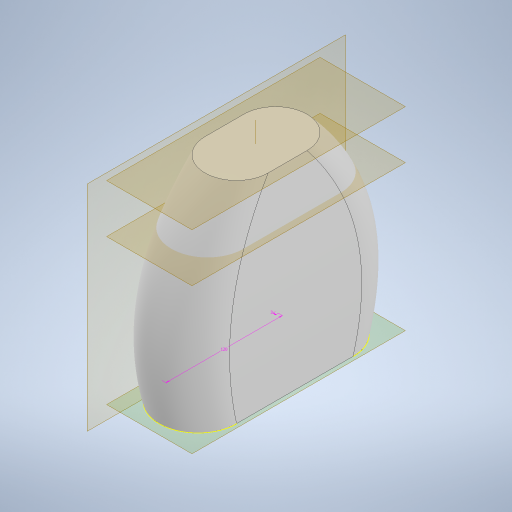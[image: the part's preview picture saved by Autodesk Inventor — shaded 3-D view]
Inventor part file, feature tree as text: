
AUTODESK INVENTOR PART (.ipt)
format: ipt  version: 2023 (Build 270158000, 158)  size: 420,864 bytes
history: native  units: mm
features: sketch x4, plane x4, loft x1, shell x1, extrude x1, projected_geometry x1
ambient origin geometry x8: Origin, YZ Plane, XZ Plane, XY Plane, X Axis, Y Axis, Z Axis, Center Point
bodies: Solid1 (feature_tree)
feature tree (12):
  sketch  "Sketch1"  dims[d0=120.0mm d1=80.0mm d2=20.0mm]
  plane  "Work Plane1"
  sketch  "Sketch2"  dims[d3=200.0mm d4=40.0mm]
  plane  "Work Plane2"
  sketch  "Sketch3"  dims[d5=65.0mm]
  plane  "Work Plane3"
  loft  "Loft1"
  shell  "Shell1"  Thickness=20.0mm
  plane  "Work Plane4"
  extrude  "Extrusion1"  Depth=40.0mm
  sketch  "Sketch9"  dims[d6=150.0mm d7=100.0mm d8=75.0mm d9=0.0mm d10=90.0deg d11=0.0mm d12=90.0deg d13=0.0mm d14=90.0deg d15=3.0mm d16=3.0mm d17=120.0mm d19=21.0mm d20=10.0mm d21=0.0mm]
  projected_geometry  "Projected Loop1"
